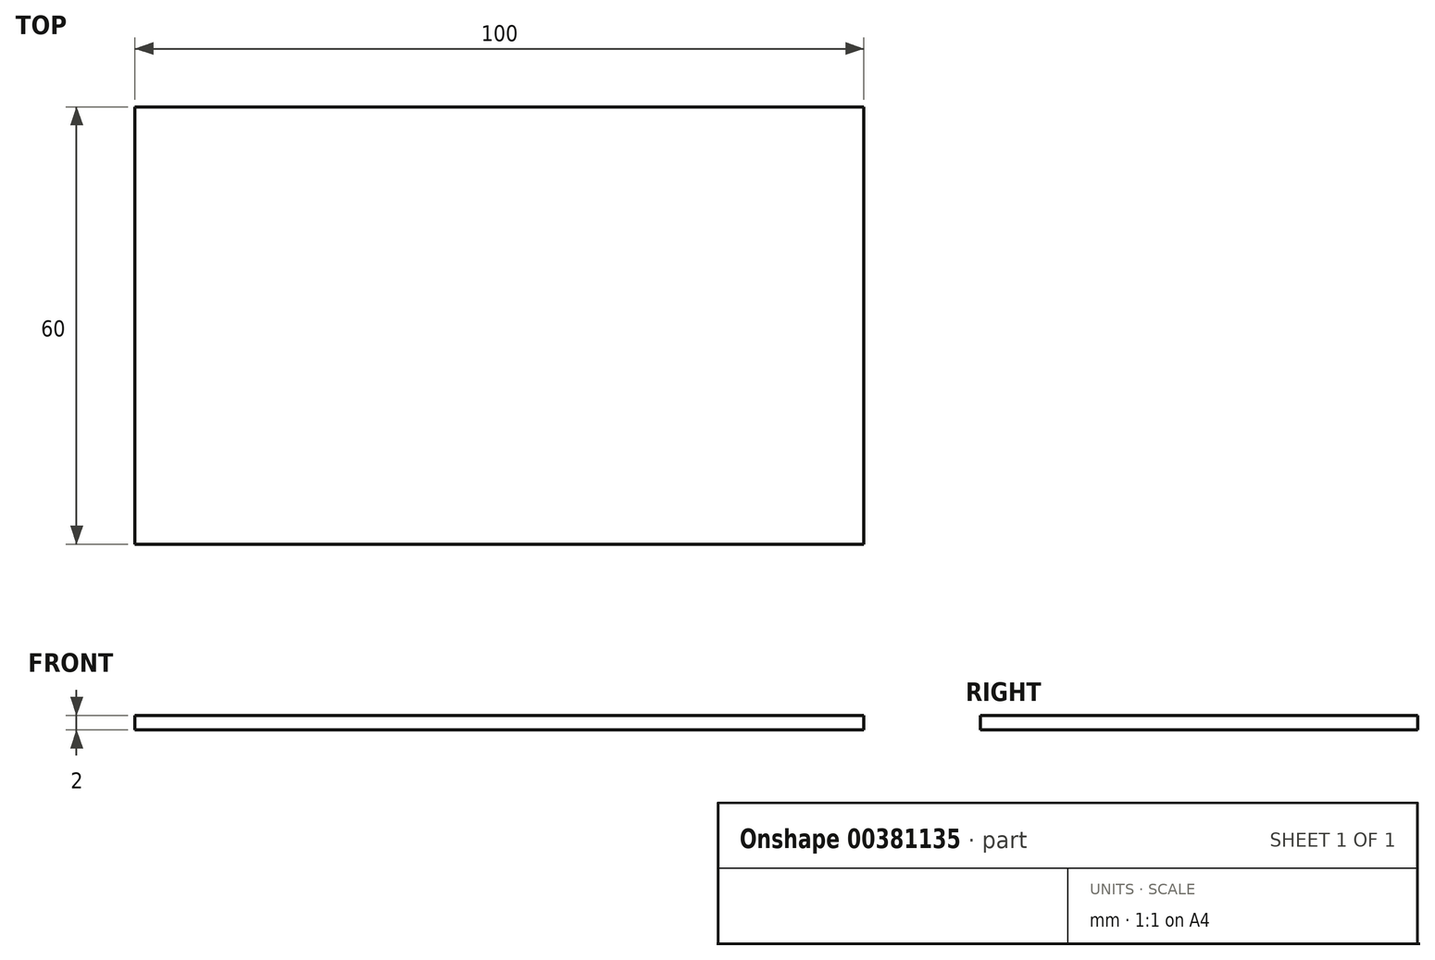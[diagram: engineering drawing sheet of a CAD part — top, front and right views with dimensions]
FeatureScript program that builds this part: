
annotation { "Feature Type Name" : "Feature", "Feature Type Description" : "" }
export const myFeature = defineFeature(function(context is Context, id is Id, definition is map)
    precondition{}
    {
        {
            var Q0;
            Q0=qCreatedBy(makeId("Top.planeOp"),FACE);
            var sketch = newSketch(context, id + "F0", { "sketchPlane" : qUnion([Q0])});
            skLineSegment(sketch, "E0.bottom", {"start": v(50, -30) * mm, "end": v(-50, -30) * mm});
            skLineSegment(sketch, "E0.top", {"start": v(50, 30) * mm, "end": v(-50, 30) * mm});
            skLineSegment(sketch, "E0.left", {"start": v(50, -30) * mm, "end": v(50, 30) * mm});
            skLineSegment(sketch, "E0.right", {"start": v(-50, -30) * mm, "end": v(-50, 30) * mm});
            skPoint(sketch, "E0.middle", {"position": v(0, 0) * mm});
            skSolve(sketch);
        }
        {
            var Q0;
            Q0 = qSketchRegion(id + "F0", true);
            extrude(context, id + "F1", {"entities" : qUnion([Q0]), "depth" : 2 * mm});
        }
    });
